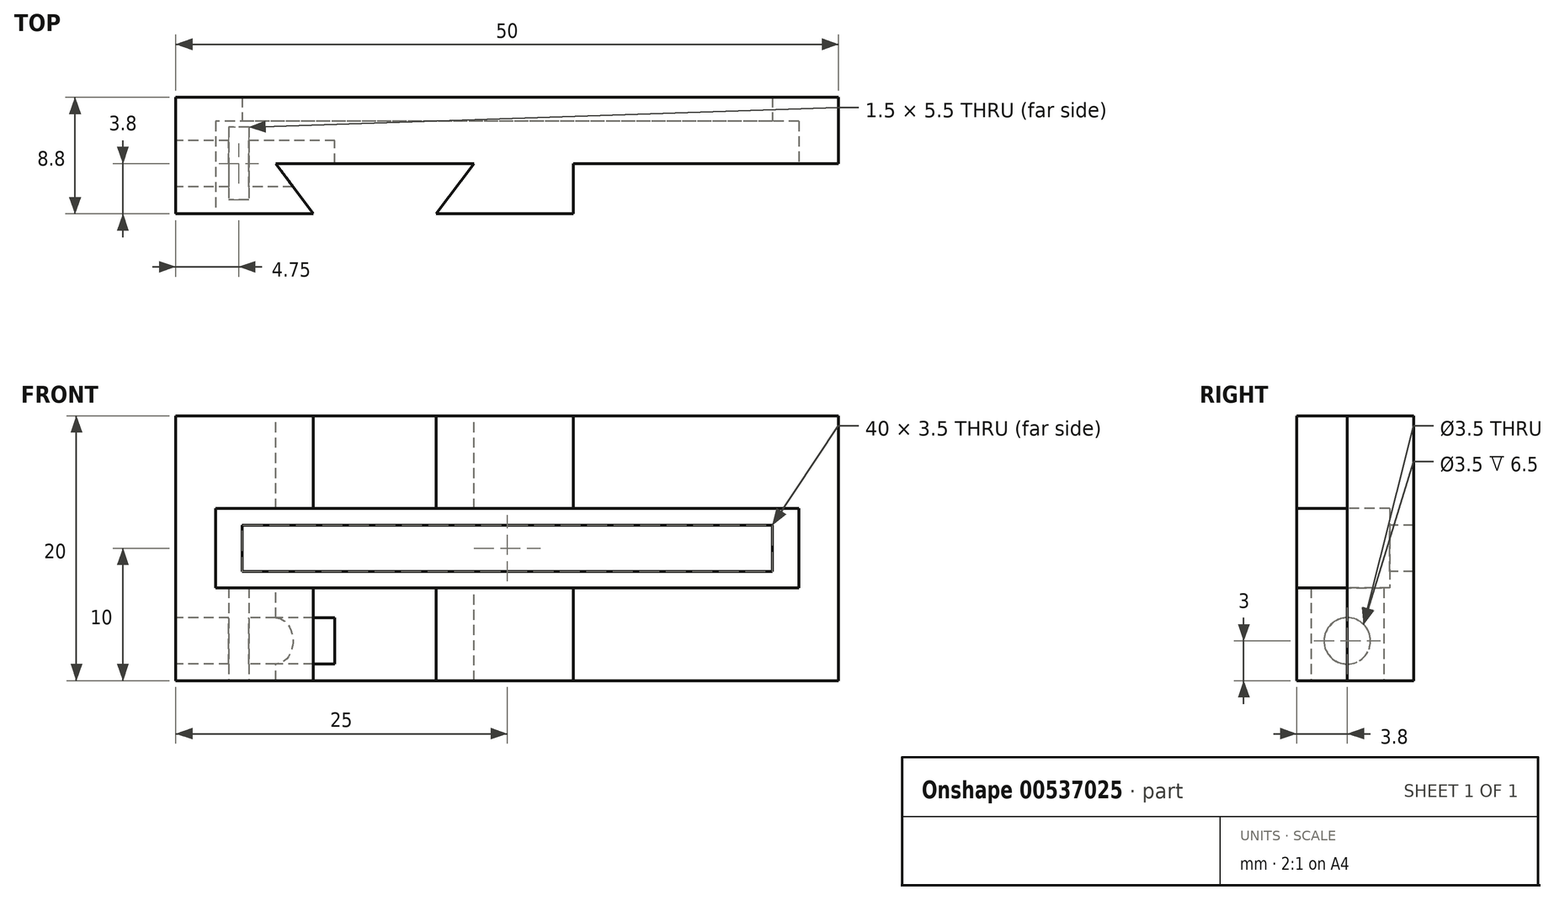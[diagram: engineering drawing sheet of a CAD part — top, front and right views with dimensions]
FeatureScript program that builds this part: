
annotation { "Feature Type Name" : "Feature", "Feature Type Description" : "" }
export const myFeature = defineFeature(function(context is Context, id is Id, definition is map)
    precondition{}
    {
        {
            var Q0;
            Q0=qCreatedBy(makeId("Front.planeOp"),FACE);
            var sketch = newSketch(context, id + "F0", { "sketchPlane" : qUnion([Q0])});
            skLineSegment(sketch, "E0.bottom", {"start": v(25, 10) * mm, "end": v(-25, 10) * mm});
            skLineSegment(sketch, "E0.top", {"start": v(25, -10) * mm, "end": v(-25, -10) * mm});
            skLineSegment(sketch, "E0.left", {"start": v(25, 10) * mm, "end": v(25, -10) * mm});
            skLineSegment(sketch, "E0.right", {"start": v(-25, 10) * mm, "end": v(-25, -10) * mm});
            skPoint(sketch, "E0.middle", {"position": v(0, 0) * mm});
            skSolve(sketch);
        }
        {
            var Q0;
            Q0=makeQuery(id+"F0.imprint","IMPRINT",FACE,{"disambiguationData":[TD([[makeQuery(id+"F0.imprint","IMPRINT",EDGE,{"derivedFrom":sQuery(id+"F0.wireOp",EDGE,"E0.bottom")}),1.0]])]});
            extrude(context, id + "F1", {"entities" : qUnion([Q0]), "depth" : 5 * mm, "offsetDistance" : 25 * mm});
        }
        {
            var Q0;
            Q0=makeQuery(id+"F1.opExtrude","CAP_FACE",FACE,{"disambiguationData":[OSD([sQuery(id+"F0.wireOp",EDGE,"E0.bottom"),sQuery(id+"F0.wireOp",EDGE,"E0.top"),sQuery(id+"F0.wireOp",EDGE,"E0.left"),sQuery(id+"F0.wireOp",EDGE,"E0.right")])],"isStart":false});
            var sketch = newSketch(context, id + "F2", { "sketchPlane" : qUnion([Q0])});
            skLineSegment(sketch, "E1.bottom", {"start": v(5, 10) * mm, "end": v(-25, 10) * mm});
            skLineSegment(sketch, "E1.top", {"start": v(5, -10) * mm, "end": v(-25, -10) * mm});
            skLineSegment(sketch, "E1.left", {"start": v(5, 10) * mm, "end": v(5, -10) * mm});
            skLineSegment(sketch, "E1.right", {"start": v(-25, 10) * mm, "end": v(-25, -10) * mm});
            skPoint(sketch, "E1.middle", {"position": v(-10, 0) * mm});
            skSolve(sketch);
        }
        {
            var Q0;
            Q0 = qSketchRegion(id + "F2", true);
            extrude(context, id + "F3", {"entities" : qUnion([Q0]), "depth" : 3.8 * mm, "offsetDistance" : 25 * mm});
        }
        {
            var Q0;
            Q0=makeQuery(id+"F3.opExtrude","CAP_FACE",FACE,{"disambiguationData":[OSD([sQuery(id+"F2.wireOp",EDGE,"E1.bottom"),sQuery(id+"F2.wireOp",EDGE,"E1.top"),sQuery(id+"F2.wireOp",EDGE,"E1.left"),sQuery(id+"F2.wireOp",EDGE,"E1.right")])],"isStart":false});
            var sketch = newSketch(context, id + "F4", { "sketchPlane" : qUnion([Q0])});
            skLineSegment(sketch, "E2.bottom", {"start": v(-2.37, 10) * mm, "end": v(-17.62, 10) * mm});
            skLineSegment(sketch, "E2.top", {"start": v(-2.37, -10) * mm, "end": v(-17.62, -10) * mm});
            skLineSegment(sketch, "E2.left", {"start": v(-2.37, 10) * mm, "end": v(-2.37, -10) * mm});
            skLineSegment(sketch, "E2.right", {"start": v(-17.62, 10) * mm, "end": v(-17.62, -10) * mm});
            skPoint(sketch, "E2.middle", {"position": v(0, 0) * mm});
            skSolve(sketch);
        }
        {
            var Q0;
            Q0=makeQuery(id+"F4.imprint","IMPRINT",FACE,{"disambiguationData":[TD([[makeQuery(id+"F4.imprint","IMPRINT",EDGE,{"derivedFrom":sQuery(id+"F4.wireOp",EDGE,"E2.bottom")}),1.0]])]});
            extrude(context, id + "F5", {"entities" : qUnion([Q0]), "oppositeDirection" : true, "depth" : 4 * mm, "offsetDistance" : 25 * mm});
        }
        {
            var Q0;
            Q0=makeQuery(id+"F5.opExtrude","CAP_EDGE",EDGE,{"disambiguationData":[OSD([sQuery(id+"F4.wireOp",EDGE,"E2.left")])],"isStart":true});
            var Q1;
            Q1=makeQuery(id+"F5.opExtrude","CAP_EDGE",EDGE,{"disambiguationData":[OSD([sQuery(id+"F4.wireOp",EDGE,"E2.right")])],"isStart":true});
            chamfer(context, id + "F6", {"entities" : qUnion([Q0, Q1]), "chamferType" : ChamferType.TWO_OFFSETS, "width1" : 3 * mm, "oppositeDirection" : true, "width2" : 4 * mm, "tangentPropagation" : true});
        }
        {
            var Q0;
            Q0=makeQuery(id+"F5.opExtrude","SWEPT_BODY",BODY,{"disambiguationData":[OSD([sQuery(id+"F4.wireOp",EDGE,"E2.bottom"),sQuery(id+"F4.wireOp",EDGE,"E2.top"),sQuery(id+"F4.wireOp",EDGE,"E2.left"),sQuery(id+"F4.wireOp",EDGE,"E2.right")])]});
            var Q1;
            Q1=makeQuery(id+"F3.opExtrude","SWEPT_BODY",BODY,{"disambiguationData":[OSD([sQuery(id+"F2.wireOp",EDGE,"E1.bottom"),sQuery(id+"F2.wireOp",EDGE,"E1.top"),sQuery(id+"F2.wireOp",EDGE,"E1.left"),sQuery(id+"F2.wireOp",EDGE,"E1.right")])]});
            booleanBodies(context, id + "F7", {"operationType" : BooleanOperationType.SUBTRACTION, "tools" : qUnion([Q0]), "targets" : qUnion([Q1])});
        }
        {
            var Q0;
            Q0=makeQuery(id+"F1.opExtrude","SWEPT_BODY",BODY,{"disambiguationData":[OSD([sQuery(id+"F0.wireOp",EDGE,"E0.bottom"),sQuery(id+"F0.wireOp",EDGE,"E0.top"),sQuery(id+"F0.wireOp",EDGE,"E0.left"),sQuery(id+"F0.wireOp",EDGE,"E0.right")])]});
            var Q1;
            Q1=makeQuery(id+"F7.opBoolean","SPLIT",BODY,{"disambiguationData":[OD(0.0)],"derivedFrom":makeQuery(id+"F3.opExtrude","SWEPT_BODY",BODY,{"disambiguationData":[OSD([sQuery(id+"F2.wireOp",EDGE,"E1.bottom"),sQuery(id+"F2.wireOp",EDGE,"E1.top"),sQuery(id+"F2.wireOp",EDGE,"E1.left"),sQuery(id+"F2.wireOp",EDGE,"E1.right")])]})});
            var Q2;
            Q2=makeQuery(id+"F7.opBoolean","SPLIT",BODY,{"disambiguationData":[OD(1.0)],"derivedFrom":makeQuery(id+"F3.opExtrude","SWEPT_BODY",BODY,{"disambiguationData":[OSD([sQuery(id+"F2.wireOp",EDGE,"E1.bottom"),sQuery(id+"F2.wireOp",EDGE,"E1.top"),sQuery(id+"F2.wireOp",EDGE,"E1.left"),sQuery(id+"F2.wireOp",EDGE,"E1.right")])]})});
            booleanBodies(context, id + "F8", {"operationType" : BooleanOperationType.UNION, "tools" : qUnion([Q0, Q1, Q2])});
        }
        {
            var Q0;
            {var subQ0=sQuery(id+"F2.wireOp",EDGE,"E1.bottom");var subQ1=sQuery(id+"F2.wireOp",EDGE,"E1.right");var subQ2=sQuery(id+"F2.wireOp",EDGE,"E1.top");Q0=makeQuery(id+"F7.opBoolean","SPLIT",FACE,{"disambiguationData":[TD([makeQuery(id+"F3.opExtrude","SWEPT_FACE",FACE,{"disambiguationData":[OSD([subQ1])]})])],"derivedFrom":makeQuery(id+"F3.opExtrude","CAP_FACE",FACE,{"disambiguationData":[OSD([subQ0,subQ2,sQuery(id+"F2.wireOp",EDGE,"E1.left"),subQ1])],"isStart":false})});}
            var sketch = newSketch(context, id + "F9", { "sketchPlane" : qUnion([Q0])});
            skLineSegment(sketch, "E3.bottom", {"start": v(-20, 1.75) * mm, "end": v(20, 1.75) * mm});
            skLineSegment(sketch, "E3.top", {"start": v(-20, -1.75) * mm, "end": v(20, -1.75) * mm});
            skLineSegment(sketch, "E3.left", {"start": v(-20, 1.75) * mm, "end": v(-20, -1.75) * mm});
            skLineSegment(sketch, "E3.right", {"start": v(20, 1.75) * mm, "end": v(20, -1.75) * mm});
            skPoint(sketch, "E3.middle", {"position": v(0, 0) * mm});
            skSolve(sketch);
        }
        {
            var Q0;
            Q0 = qSketchRegion(id + "F9", true);
            extrude(context, id + "F10", {"entities" : qUnion([Q0]), "operationType" : NewBodyOperationType.REMOVE, "endBound" : BoundingType.SYMMETRIC, "oppositeDirection" : true, "depth" : 25 * mm, "offsetDistance" : 25 * mm});
        }
        {
            var Q0;
            {var subQ0=sQuery(id+"F2.wireOp",EDGE,"E1.bottom");var subQ1=sQuery(id+"F2.wireOp",EDGE,"E1.right");var subQ2=sQuery(id+"F2.wireOp",EDGE,"E1.top");Q0=makeQuery(id+"F7.opBoolean","SPLIT",FACE,{"disambiguationData":[TD([makeQuery(id+"F3.opExtrude","SWEPT_FACE",FACE,{"disambiguationData":[OSD([subQ1])]})])],"derivedFrom":makeQuery(id+"F3.opExtrude","CAP_FACE",FACE,{"disambiguationData":[OSD([subQ0,subQ2,sQuery(id+"F2.wireOp",EDGE,"E1.left"),subQ1])],"isStart":false})});}
            var sketch = newSketch(context, id + "F11", { "sketchPlane" : qUnion([Q0])});
            skLineSegment(sketch, "E4.bottom", {"start": v(22, 3) * mm, "end": v(-22, 3) * mm});
            skLineSegment(sketch, "E4.top", {"start": v(22, -3) * mm, "end": v(-22, -3) * mm});
            skLineSegment(sketch, "E4.left", {"start": v(22, 3) * mm, "end": v(22, -3) * mm});
            skLineSegment(sketch, "E4.right", {"start": v(-22, 3) * mm, "end": v(-22, -3) * mm});
            skPoint(sketch, "E4.middle", {"position": v(0, 0) * mm});
            skSolve(sketch);
        }
        {
            var Q0;
            Q0 = qSketchRegion(id + "F11", true);
            extrude(context, id + "F12", {"entities" : qUnion([Q0]), "operationType" : NewBodyOperationType.REMOVE, "oppositeDirection" : true, "depth" : 7 * mm, "offsetDistance" : 25 * mm});
        }
        {
            var Q0;
            Q0=makeQuery(id+"F8.opBoolean","MERGE",FACE,{"derivedFrom":[makeQuery(id+"F1.opExtrude","SWEPT_FACE",FACE,{"disambiguationData":[OSD([sQuery(id+"F0.wireOp",EDGE,"E0.right")])]}),makeQuery(id+"F3.opExtrude","SWEPT_FACE",FACE,{"disambiguationData":[OSD([sQuery(id+"F2.wireOp",EDGE,"E1.right")])]})]});
            var sketch = newSketch(context, id + "F13", { "sketchPlane" : qUnion([Q0])});
            skCircle(sketch, "E5", {"center": v(5, -7) * mm, "radius": 1.75 * mm});
            skSolve(sketch);
        }
        {
            var Q0;
            Q0=makeQuery(id+"F13.imprint","IMPRINT",FACE,{"disambiguationData":[TD([[makeQuery(id+"F13.imprint","IMPRINT",EDGE,{"derivedFrom":sQuery(id+"F13.wireOp",EDGE,"E5")}),1.0]])]});
            extrude(context, id + "F14", {"entities" : qUnion([Q0]), "operationType" : NewBodyOperationType.REMOVE, "oppositeDirection" : true, "depth" : 12 * mm, "offsetDistance" : 25 * mm});
        }
        {
            var Q0;
            {var subQ0=sQuery(id+"F2.wireOp",EDGE,"E1.right");var subQ1=sQuery(id+"F2.wireOp",EDGE,"E1.left");var subQ2=sQuery(id+"F2.wireOp",EDGE,"E1.top");var subQ6=makeQuery(id+"F3.opExtrude","SWEPT_FACE",FACE,{"disambiguationData":[OSD([subQ2])]});Q0=makeQuery(id+"F8.opBoolean","MERGE",FACE,{"derivedFrom":[makeQuery(id+"F1.opExtrude","SWEPT_FACE",FACE,{"disambiguationData":[OSD([sQuery(id+"F0.wireOp",EDGE,"E0.top")])]}),makeQuery(id+"F7.opBoolean","SPLIT",FACE,{"disambiguationData":[TD([makeQuery(id+"F3.opExtrude","SWEPT_FACE",FACE,{"disambiguationData":[OSD([subQ1])]})])],"derivedFrom":subQ6}),makeQuery(id+"F7.opBoolean","SPLIT",FACE,{"disambiguationData":[TD([makeQuery(id+"F3.opExtrude","SWEPT_FACE",FACE,{"disambiguationData":[OSD([subQ0])]})])],"derivedFrom":subQ6})]});}
            var sketch = newSketch(context, id + "F15", { "sketchPlane" : qUnion([Q0])});
            skLineSegment(sketch, "E6.bottom", {"start": v(-19.5, 2.25) * mm, "end": v(-21, 2.25) * mm});
            skLineSegment(sketch, "E6.top", {"start": v(-19.5, 7.75) * mm, "end": v(-21, 7.75) * mm});
            skLineSegment(sketch, "E6.left", {"start": v(-19.5, 2.25) * mm, "end": v(-19.5, 7.75) * mm});
            skLineSegment(sketch, "E6.right", {"start": v(-21, 2.25) * mm, "end": v(-21, 7.75) * mm});
            skPoint(sketch, "E6.middle", {"position": v(-20.25, 5) * mm});
            skSolve(sketch);
        }
        {
            var Q0;
            Q0=makeQuery(id+"F15.imprint","IMPRINT",FACE,{"disambiguationData":[TD([[makeQuery(id+"F15.imprint","IMPRINT",EDGE,{"derivedFrom":sQuery(id+"F15.wireOp",EDGE,"E6.bottom")}),-1.0]])]});
            extrude(context, id + "F16", {"entities" : qUnion([Q0]), "operationType" : NewBodyOperationType.REMOVE, "oppositeDirection" : true, "depth" : 8 * mm, "offsetDistance" : 25 * mm});
        }
    });
